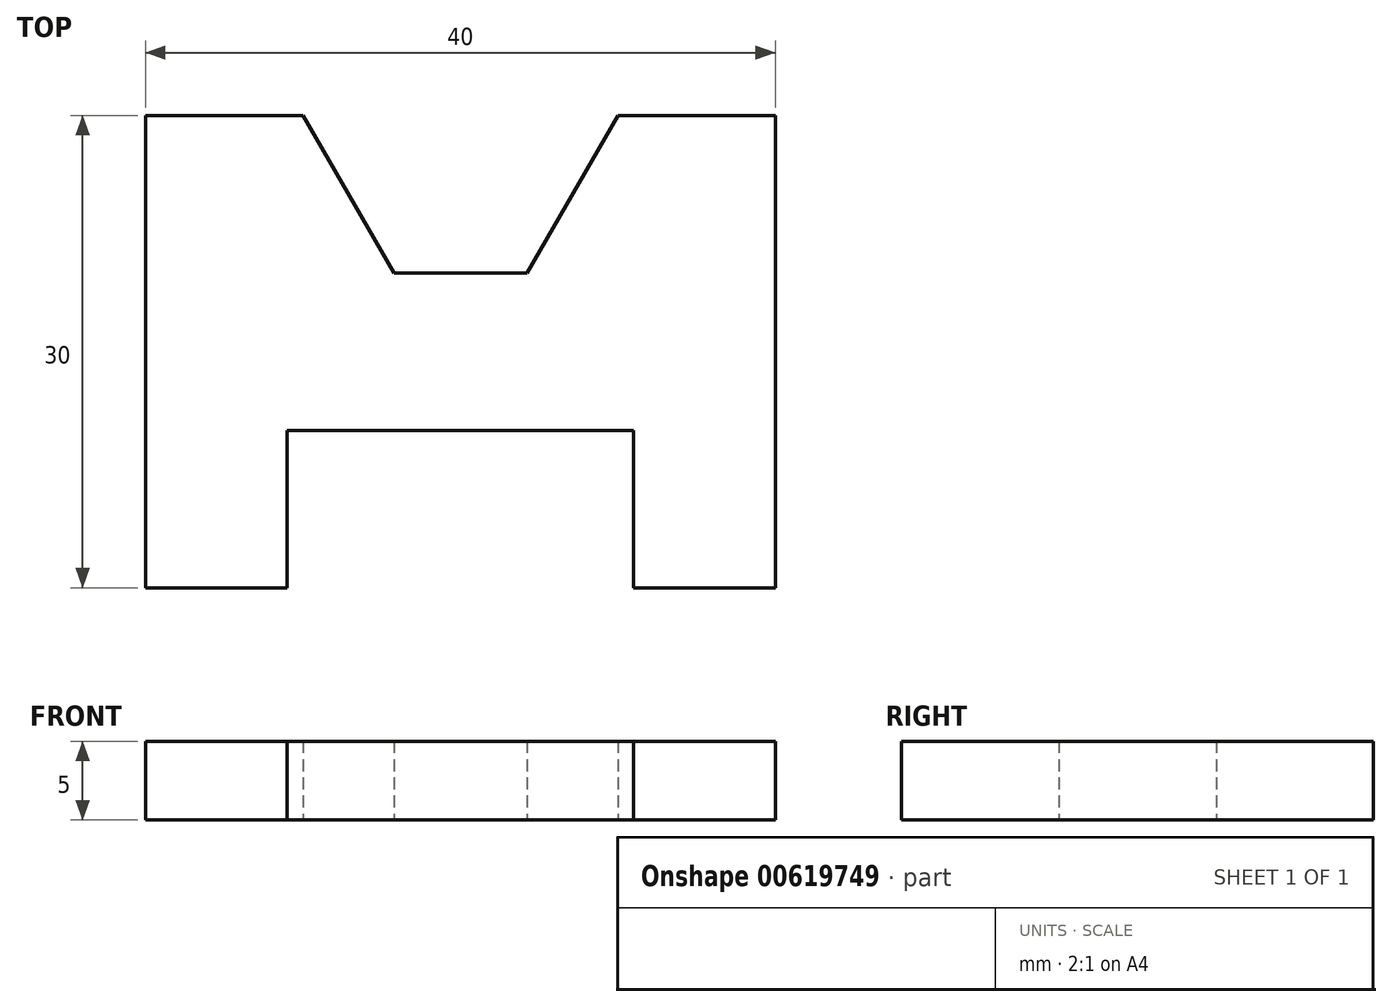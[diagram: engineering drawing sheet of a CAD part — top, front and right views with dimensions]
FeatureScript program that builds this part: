
annotation { "Feature Type Name" : "Feature", "Feature Type Description" : "" }
export const myFeature = defineFeature(function(context is Context, id is Id, definition is map)
    precondition{}
    {
        {
            var Q0;
            Q0=qCreatedBy(makeId("Top.planeOp"),FACE);
            var sketch = newSketch(context, id + "F0", { "sketchPlane" : qUnion([Q0])});
            skLineSegment(sketch, "E0", {"start": v(0, 0) * mm, "end": v(0, 26.66) * mm, "construction": true});
            skLineSegment(sketch, "E1", {"start": v(0, 18.54) * mm, "end": v(-4.23, 18.54) * mm});
            skLineSegment(sketch, "E2", {"start": v(-10, 28.54) * mm, "end": v(-4.23, 18.54) * mm});
            skLineSegment(sketch, "E3", {"start": v(-10, 28.54) * mm, "end": v(-20, 28.54) * mm});
            skLineSegment(sketch, "E4", {"start": v(-20, 28.54) * mm, "end": v(-20, -1.46) * mm});
            skLineSegment(sketch, "E5", {"start": v(-20, -1.46) * mm, "end": v(-11, -1.46) * mm});
            skLineSegment(sketch, "E6", {"start": v(-11, -1.46) * mm, "end": v(-11, 8.54) * mm});
            skLineSegment(sketch, "E7", {"start": v(-11, 8.54) * mm, "end": v(0, 8.54) * mm});
            skLineSegment(sketch, "E8.MirrorCS", {"start": v(0, 18.54) * mm, "end": v(4.23, 18.54) * mm});
            skLineSegment(sketch, "E9.MirrorCS", {"start": v(10, 28.54) * mm, "end": v(4.23, 18.54) * mm});
            skLineSegment(sketch, "E10.MirrorCS", {"start": v(10, 28.54) * mm, "end": v(20, 28.54) * mm});
            skLineSegment(sketch, "E11.MirrorCS", {"start": v(20, 28.54) * mm, "end": v(20, -1.46) * mm});
            skLineSegment(sketch, "E12.MirrorCS", {"start": v(20, -1.46) * mm, "end": v(11, -1.46) * mm});
            skLineSegment(sketch, "E13.MirrorCS", {"start": v(11, -1.46) * mm, "end": v(11, 8.54) * mm});
            skLineSegment(sketch, "E14.MirrorCS", {"start": v(11, 8.54) * mm, "end": v(0, 8.54) * mm});
            skSolve(sketch);
        }
        {
            var Q0;
            Q0=makeQuery(id+"F0.imprint","IMPRINT",FACE,{"disambiguationData":[TD([[makeQuery(id+"F0.imprint","IMPRINT",EDGE,{"derivedFrom":sQuery(id+"F0.wireOp",EDGE,"E1")}),1.0]])]});
            extrude(context, id + "F1", {"entities" : qUnion([Q0]), "depth" : 5 * mm, "offsetDistance" : 25 * mm});
        }
    });
